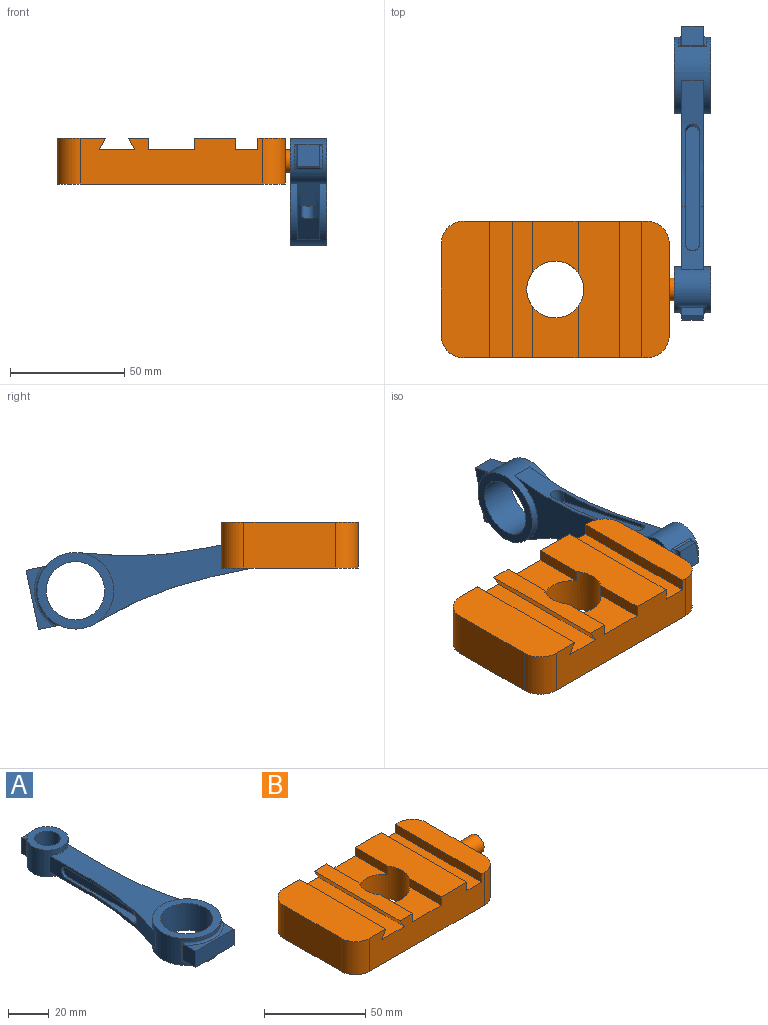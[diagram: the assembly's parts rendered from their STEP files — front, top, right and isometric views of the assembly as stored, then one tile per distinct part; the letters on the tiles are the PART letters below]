
ASSEMBLY  parts=2 mates=1
PART A: 42 faces, bbox 33.7x129.5x16.1 mm
  f0: plane 10x2.64mm, normal (0,0,1), area 18.4mm2, adj f6,f7,f30,f31
  f1: plane 10x2.64mm, normal (0,0,-1), area 18.4mm2, adj f6,f7,f29,f31
  f2: plane 82.69x31.66mm, normal (0,0,1), area 1120mm2, adj f8,f9,f10,f11,f32,f33
  f3: plane 82.69x31.66mm, normal (0,0,-1), area 1120mm2, adj f8,f9,f10,f11,f32,f33
  f4: cylinder r=12.8mm len=25.6mm, axis (0,0,-1), area 1286.8mm2, adj f16,f17
  f5: cylinder r=6.25mm len=16mm, axis (0,0,-1), area 628.3mm2, adj f18,f19
  f6: plane 10x9.6mm, normal (0,1,0), area 96mm2, adj f0,f1,f7,f31
  f7: plane 9.95x3.34mm, normal (-1,0,0), area 32.1mm2, adj f0,f1,f6,f28,f29,f30
  f8: cylinder r=10mm len=20mm, axis (0,0,-1), area 731.2mm2, adj f2,f3,f9,f18,f19,f28,f29,f30
  f9: plane 28x9.6mm, normal (-1,0,0), area 147.2mm2, adj f2,f3,f8,f10,f21,f22,f24
  f10: cylinder r=163.3mm len=54.69mm, axis (0,0,-1), area 305.5mm2, adj f2,f3,f9,f11,f21,f22,f23
  f11: cylinder r=16.8mm len=33.6mm, axis (0,0,-1), area 914.8mm2, adj f2,f3,f10,f16,f17,f25,f26,f27
  f12: plane 10.6x8.73mm, normal (-1,0,0), area 83.7mm2, adj f13,f14,f15,f25,f26,f27
  f13: plane 26.6x9.6mm, normal (0,-1,0), area 255.4mm2, adj f12,f14,f15,f34
  f14: plane 26.6x7.21mm, normal (0,0,1), area 83.7mm2, adj f12,f13,f27,f34
  f15: plane 26.6x7.21mm, normal (0,0,-1), area 83.7mm2, adj f12,f13,f25,f34
  f16: plane 33.6x33.6mm, normal (0,0,-1), area 372mm2, adj f4,f11
  f17: plane 33.6x33.6mm, normal (0,0,1), area 372mm2, adj f4,f11
  f18: plane 20x20mm, normal (0,0,-1), area 191.4mm2, adj f5,f8
  f19: plane 20x20mm, normal (0,0,1), area 191.4mm2, adj f5,f8
  f20: plane 56x6.4mm, normal (-1,0,0), area 349.6mm2, adj f21,f22,f23,f24
  f21: plane 49.6x4.99mm, normal (0,0,1), area 116.7mm2, adj f9,f10,f20,f23,f24
  f22: plane 49.6x4.99mm, normal (0,0,-1), area 116.7mm2, adj f9,f10,f20,f23,f24
  f23: cylinder r=3.2mm len=6.4mm, axis (1,0,0), area 54.6mm2, adj f10,f20,f21,f22
  f24: cylinder r=3.2mm len=6.4mm, axis (-1,0,0), area 16.1mm2, adj f9,f20,f21,f22
  f25: torus R=18mm, axis (0,0,1), area 57.5mm2, adj f11,f12,f15,f26,f34,f40
  f26: cylinder r=1.2mm len=12mm, axis (0,0,-1), area 8.6mm2, adj f11,f12,f25,f27
  f27: torus R=18mm, axis (0,0,1), area 57.5mm2, adj f11,f12,f14,f26,f34,f40
  f28: cylinder r=1.2mm len=12mm, axis (0,0,-1), area 13mm2, adj f7,f8,f29,f30
  f29: torus R=11.2mm, axis (0,0,1), area 20.3mm2, adj f1,f7,f8,f28,f31,f41
  f30: torus R=11.2mm, axis (0,0,1), area 20.3mm2, adj f0,f7,f8,f28,f31,f41
  f31: plane 9.95x3.34mm, normal (1,0,0), area 32.1mm2, adj f0,f1,f6,f29,f30,f41
  f32: plane 28x9.6mm, normal (1,0,0), area 147.2mm2, adj f2,f3,f8,f33,f36,f37,f39
  f33: cylinder r=163.3mm len=54.69mm, axis (0,0,-1), area 305.5mm2, adj f2,f3,f11,f32,f36,f37,f38
  f34: plane 10.6x8.73mm, normal (1,0,0), area 83.7mm2, adj f13,f14,f15,f25,f27,f40
  f35: plane 56x6.4mm, normal (1,0,0), area 349.6mm2, adj f36,f37,f38,f39
  f36: plane 49.6x4.99mm, normal (0,0,1), area 116.7mm2, adj f32,f33,f35,f38,f39
  f37: plane 49.6x4.99mm, normal (0,0,-1), area 116.7mm2, adj f32,f33,f35,f38,f39
  f38: cylinder r=3.2mm len=6.4mm, axis (-1,0,0), area 54.6mm2, adj f33,f35,f36,f37
  f39: cylinder r=3.2mm len=6.4mm, axis (1,0,0), area 16.1mm2, adj f32,f35,f36,f37
  f40: cylinder r=1.2mm len=12mm, axis (0,0,-1), area 8.6mm2, adj f11,f25,f27,f34
  f41: cylinder r=1.2mm len=12mm, axis (0,0,-1), area 13mm2, adj f8,f29,f30,f31
PART B: 28 faces, bbox 115x60x20 mm
  f0: plane 60x21.21mm, normal (0,0,1), area 1229.9mm2, adj f1,f2,f8,f21,f26,f27
  f1: plane 80x20mm, normal (0,1,0), area 1385.6mm2, adj f0,f4,f5,f6,f9,f10,f11,f12
  f2: plane 80x20mm, normal (0,-1,0), area 1385.6mm2, adj f0,f4,f5,f6,f9,f13,f14,f15
  f3: cylinder r=12.5mm len=25mm, axis (0,0,-1), area 1339mm2, adj f4,f6,f9,f10,f11,f12,f13,f14
  f4: plane 60x18mm, normal (0,0,1), area 1054.5mm2, adj f1,f2,f3,f10,f13,f17
  f5: plane 60x12mm, normal (0,0,1), area 677.1mm2, adj f1,f2,f7,f16,f24,f25
  f6: plane 60x8.79mm, normal (0,0,1), area 501.7mm2, adj f1,f2,f3,f11,f14,f19
  f7: plane 40x20mm, normal (1,0,0), area 721.5mm2, adj f5,f9,f22,f24,f25
  f8: plane 40x20mm, normal (-1,0,0), area 800mm2, adj f0,f9,f26,f27
  f9: plane 100x60mm, normal (0,0,-1), area 5423.3mm2, adj f1,f2,f3,f7,f8,f24,f25,f26
  f10: plane 22.5x5mm, normal (-1,0,0), area 112.5mm2, adj f1,f3,f4,f12
  f11: plane 22.5x5mm, normal (1,0,0), area 112.5mm2, adj f1,f3,f6,f12
  f12: plane 22.5x20mm, normal (0,0,1), area 380.1mm2, adj f1,f3,f10,f11
  f13: plane 22.5x5mm, normal (-1,0,0), area 112.5mm2, adj f2,f3,f4,f15
  f14: plane 22.5x5mm, normal (1,0,0), area 112.5mm2, adj f2,f3,f6,f15
  f15: plane 22.5x20mm, normal (0,0,1), area 380.1mm2, adj f2,f3,f13,f14
  f16: plane 60x5mm, normal (-1,0,0), area 300mm2, adj f1,f2,f5,f18
  f17: plane 60x5mm, normal (1,0,0), area 300mm2, adj f1,f2,f4,f18
  f18: plane 60x10mm, normal (0,0,1), area 600mm2, adj f1,f2,f16,f17
  f19: plane 60x5mm, normal (-0.87,0,-0.5), area 346.4mm2, adj f1,f2,f6,f20
  f20: plane 60x15.77mm, normal (0,0,1), area 946.4mm2, adj f1,f2,f19,f21
  f21: plane 60x5mm, normal (0.87,0,-0.5), area 346.4mm2, adj f0,f1,f2,f20
  f22: cylinder r=5mm len=15mm, axis (-1,0,0), area 471.2mm2, adj f7,f23
  f23: plane 10x10mm, normal (1,0,0), area 78.5mm2, adj f22
  f24: cylinder r=10mm len=20mm, axis (0,0,1), area 314.2mm2, adj f2,f5,f7,f9
  f25: cylinder r=10mm len=20mm, axis (0,0,-1), area 314.2mm2, adj f1,f5,f7,f9
  f26: cylinder r=10mm len=20mm, axis (0,0,1), area 314.2mm2, adj f0,f1,f8,f9
  f27: cylinder r=10mm len=20mm, axis (0,0,-1), area 314.2mm2, adj f0,f2,f8,f9
PLACE A rot(axis=(0.71,0.07,0.71),171.5deg) t=(69.79,112.97,35.67)mm
PLACE B t=(9.59,19.07,45.65)mm fixed
MATE revolute A.f8 <-> B.f22  axis (1,0,0) through (74.59,19.07,55.65)mm
